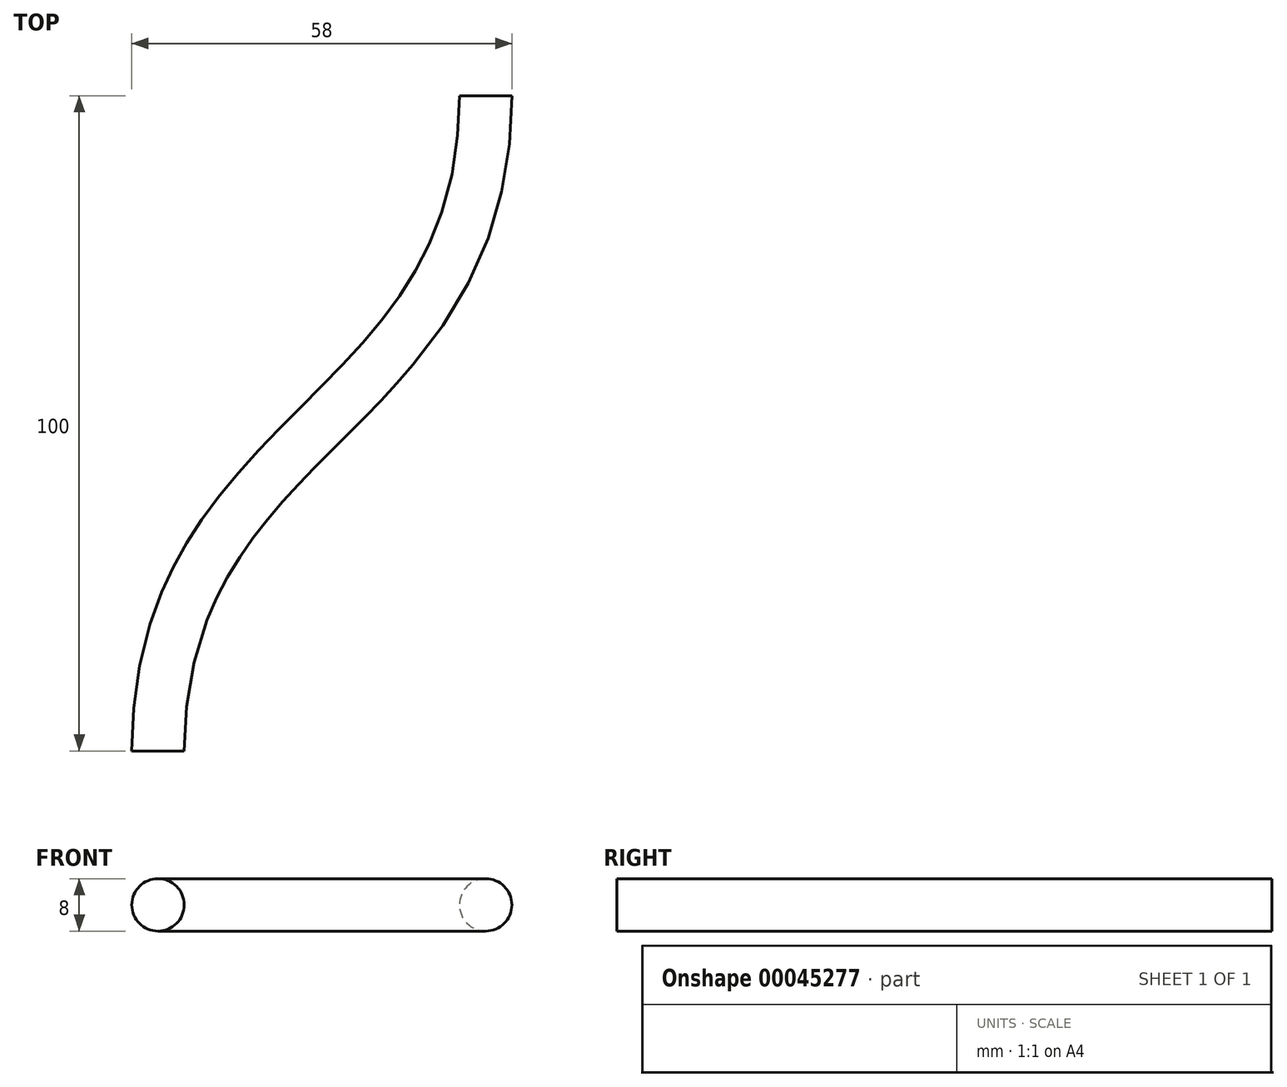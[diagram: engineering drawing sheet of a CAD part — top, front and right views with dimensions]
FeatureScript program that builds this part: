
annotation { "Feature Type Name" : "Feature", "Feature Type Description" : "" }
export const myFeature = defineFeature(function(context is Context, id is Id, definition is map)
    precondition{}
    {
        {
            var Q0;
            Q0=qCreatedBy(makeId("Top.planeOp"),FACE);
            var sketch = newSketch(context, id + "F0", { "sketchPlane" : qUnion([Q0])});
            skPoint(sketch, "E0", {"position": v(82, 0) * mm});
            skPoint(sketch, "E1", {"position": v(82, -50) * mm});
            skPoint(sketch, "E2", {"position": v(57, -50) * mm});
            skPoint(sketch, "E3", {"position": v(32, -100) * mm});
            skFitSpline(sketch, "E4", {"points": [v(82, 0) * mm, v(57, -50) * mm, v(32, -100) * mm], "startDerivative": vector(0, -150) * mm, "endDerivative": vector(0, -150) * mm});
            skSolve(sketch);
        }
        {
            var Q0;
            Q0=qCreatedBy(makeId("Front.planeOp"),FACE);
            var sketch = newSketch(context, id + "F1", { "sketchPlane" : qUnion([Q0])});
            skCircle(sketch, "E5", {"center": v(-35.45, 0) * mm, "radius": 4 * mm});
            skCircle(sketch, "E6", {"center": v(82, 0) * mm, "radius": 4 * mm});
            skSolve(sketch);
        }
        {
            var Q0;
            Q0=makeQuery(id+"F1.imprint","IMPRINT",FACE,{"disambiguationData":[TD([[makeQuery(id+"F1.imprint","IMPRINT",EDGE,{"derivedFrom":sQuery(id+"F1.wireOp",EDGE,"E6")}),1.0]])]});
            var Q1;
            Q1=sQuery(id+"F0.wireOp",EDGE,"E4");
            sweep(context, id + "F2", {"profiles" : qUnion([Q0]), "path" : qUnion([Q1])});
        }
    });
